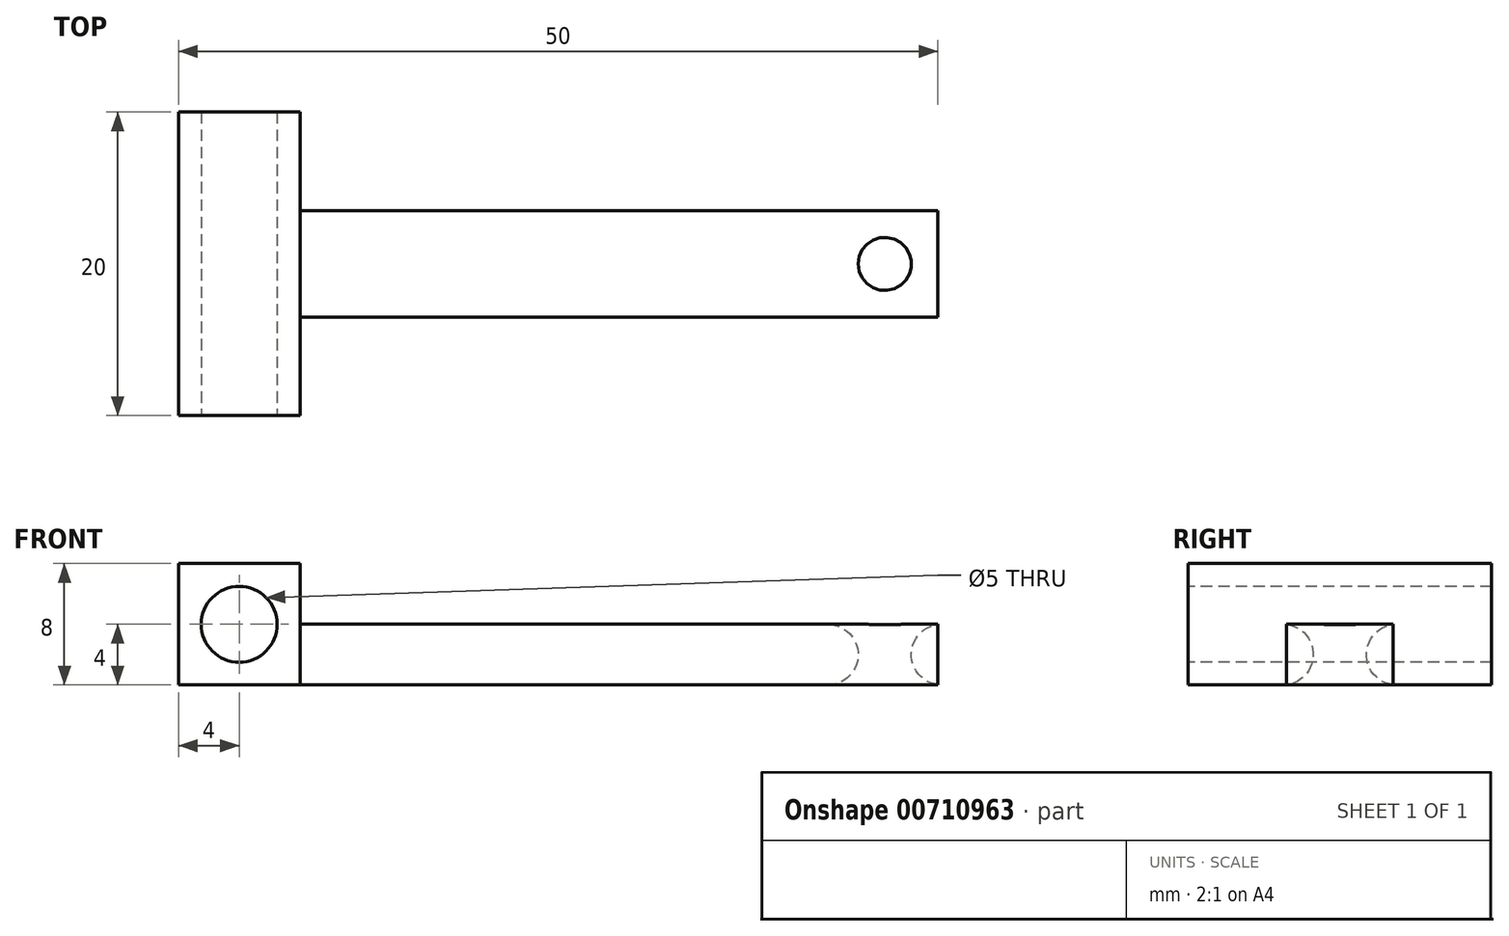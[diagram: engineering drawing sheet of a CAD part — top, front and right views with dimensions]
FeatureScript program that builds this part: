
annotation { "Feature Type Name" : "Feature", "Feature Type Description" : "" }
export const myFeature = defineFeature(function(context is Context, id is Id, definition is map)
    precondition{}
    {
        {
            var Q0;
            Q0=qCreatedBy(makeId("Top.planeOp"),FACE);
            var sketch = newSketch(context, id + "F0", { "sketchPlane" : qUnion([Q0])});
            skLineSegment(sketch, "E0.bottom", {"start": v(0, 0) * mm, "end": v(42, 0) * mm});
            skLineSegment(sketch, "E0.top", {"start": v(0, 7) * mm, "end": v(42, 7) * mm});
            skLineSegment(sketch, "E0.right", {"start": v(42, 0) * mm, "end": v(42, 7) * mm});
            skLineSegment(sketch, "E1.bottom", {"start": v(-8, 13.5) * mm, "end": v(0, 13.5) * mm});
            skLineSegment(sketch, "E1.top", {"start": v(-8, -6.5) * mm, "end": v(0, -6.5) * mm});
            skLineSegment(sketch, "E1.left", {"start": v(-8, 13.5) * mm, "end": v(-8, -6.5) * mm});
            skLineSegment(sketch, "E1.right", {"start": v(0, 13.5) * mm, "end": v(0, 7) * mm});
            skLineSegment(sketch, "E2.trimOffspring", {"start": v(0, 0) * mm, "end": v(0, -6.5) * mm});
            skCircle(sketch, "E3", {"center": v(38.5, 3.5) * mm, "radius": 1.75 * mm});
            skPoint(sketch, "E3.centerSnap0", {"position": v(42, 3.5) * mm});
            skLineSegment(sketch, "E4", {"start": v(0, 7) * mm, "end": v(0, 0) * mm});
            skSolve(sketch);
        }
        {
            var Q0;
            Q0=makeQuery(id+"F0.imprint","IMPRINT",FACE,{"disambiguationData":[TD([[makeQuery(id+"F0.imprint","IMPRINT",EDGE,{"derivedFrom":sQuery(id+"F0.wireOp",EDGE,"E1.bottom")}),-1.0]])]});
            extrude(context, id + "F1", {"entities" : qUnion([Q0]), "depth" : 8 * mm, "offsetDistance" : 25 * mm});
        }
        {
            var Q0;
            Q0=makeQuery(id+"F0.imprint","IMPRINT",FACE,{"disambiguationData":[TD([[makeQuery(id+"F0.imprint","IMPRINT",EDGE,{"derivedFrom":sQuery(id+"F0.wireOp",EDGE,"E0.bottom")}),1.0]])]});
            extrude(context, id + "F2", {"entities" : qUnion([Q0]), "operationType" : NewBodyOperationType.ADD, "depth" : 4 * mm, "offsetDistance" : 25 * mm});
        }
        {
            var Q0;
            Q0=makeQuery(id+"F2.opExtrude","CAP_EDGE",EDGE,{"disambiguationData":[OSD([sQuery(id+"F0.wireOp",EDGE,"E3")])],"isStart":false});
            var Q1;
            Q1=makeQuery(id+"F2.opExtrude","CAP_EDGE",EDGE,{"disambiguationData":[OSD([sQuery(id+"F0.wireOp",EDGE,"E3")])],"isStart":true});
            fillet(context, id + "F3", {"entities" : qUnion([Q0, Q1]), "radius" : 2 * mm, "allowEdgeOverflow" : false});
        }
        {
            var Q0;
            Q0=makeQuery(id+"F1.opExtrude","SWEPT_FACE",FACE,{"disambiguationData":[OSD([sQuery(id+"F0.wireOp",EDGE,"E1.top")])]});
            var sketch = newSketch(context, id + "F4", { "sketchPlane" : qUnion([Q0])});
            skCircle(sketch, "E5", {"center": v(-4, 4) * mm, "radius": 2.5 * mm});
            skPoint(sketch, "E5.centerSnap0", {"position": v(-4, 8) * mm});
            skPoint(sketch, "E6", {"position": v(0, 4) * mm});
            skSolve(sketch);
        }
        {
            var Q0;
            Q0 = qSketchRegion(id + "F4", true);
            extrude(context, id + "F5", {"entities" : qUnion([Q0]), "operationType" : NewBodyOperationType.REMOVE, "endBound" : BoundingType.THROUGH_ALL, "oppositeDirection" : true, "depth" : 25 * mm, "offsetDistance" : 25 * mm});
        }
    });
